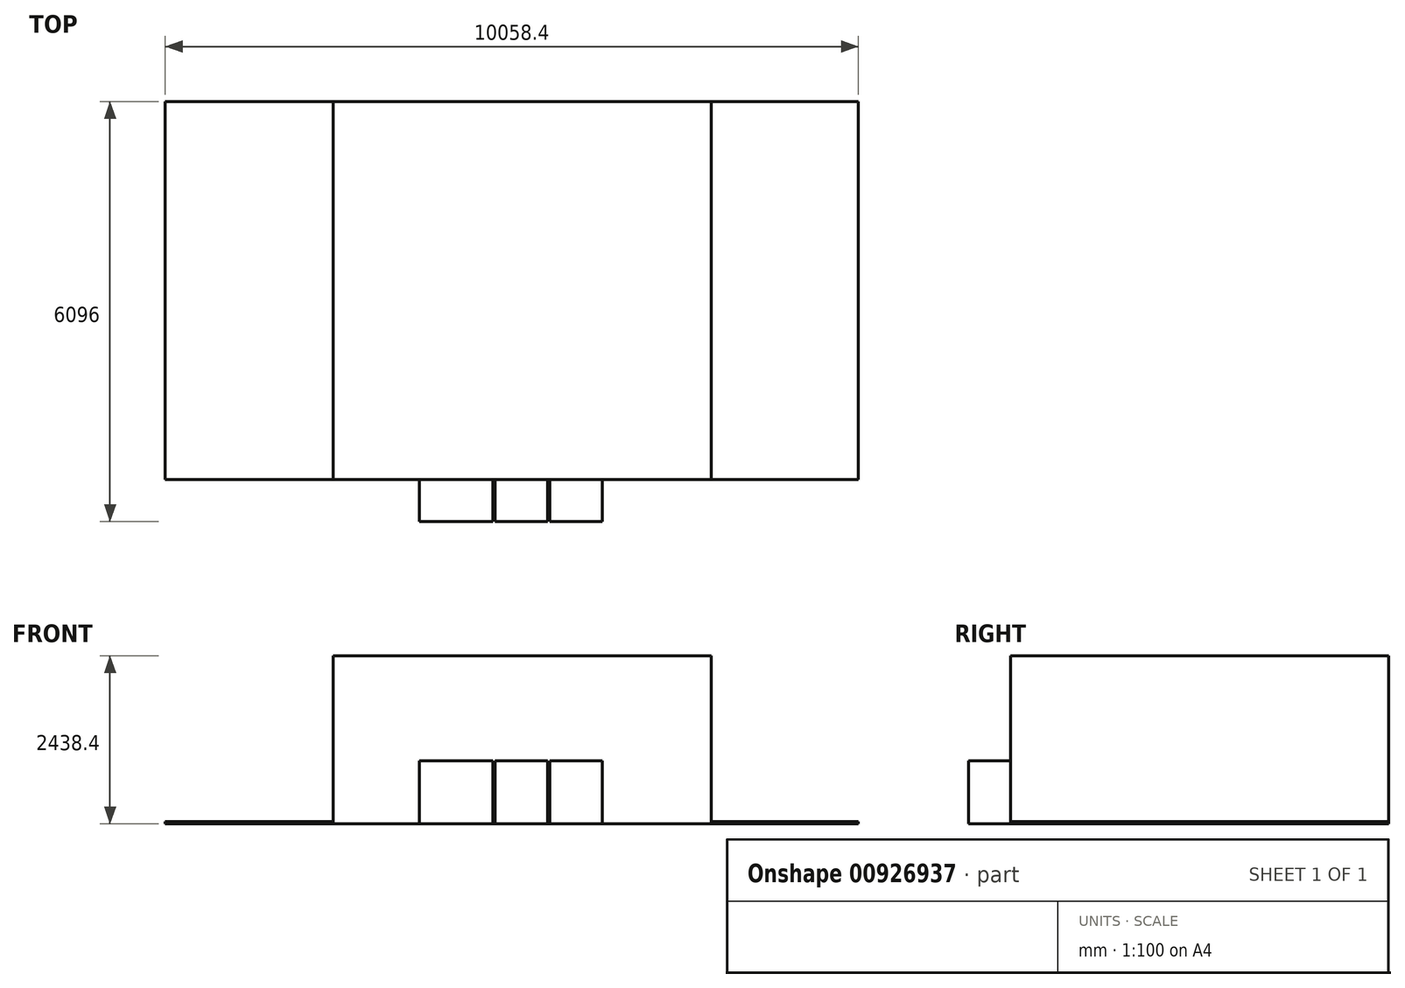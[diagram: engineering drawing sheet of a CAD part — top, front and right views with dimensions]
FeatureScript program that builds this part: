
annotation { "Feature Type Name" : "Feature", "Feature Type Description" : "" }
export const myFeature = defineFeature(function(context is Context, id is Id, definition is map)
    precondition{}
    {
        {
            var Q0;
            Q0=qCreatedBy(makeId("Top.planeOp"),FACE);
            var sketch = newSketch(context, id + "F0", { "sketchPlane" : qUnion([Q0])});
            skLineSegment(sketch, "E0.bottom", {"start": v(2743.2, 2743.2) * mm, "end": v(-2743.2, 2743.2) * mm});
            skLineSegment(sketch, "E0.top", {"start": v(2743.2, -2743.2) * mm, "end": v(-2743.2, -2743.2) * mm});
            skLineSegment(sketch, "E0.left", {"start": v(2743.2, 2743.2) * mm, "end": v(2743.2, -2743.2) * mm});
            skLineSegment(sketch, "E0.right", {"start": v(-2743.2, 2743.2) * mm, "end": v(-2743.2, -2743.2) * mm});
            skPoint(sketch, "E0.middle", {"position": v(0, 0) * mm});
            skSolve(sketch);
        }
        {
            var Q0;
            Q0 = qSketchRegion(id + "F0", true);
            extrude(context, id + "F1", {"entities" : qUnion([Q0]), "depth" : 2438.4 * mm, "offsetDistance" : 30.48 * mm});
        }
        {
            var Q0;
            Q0=makeQuery(id+"F1.opExtrude","SWEPT_FACE",FACE,{"disambiguationData":[OSD([sQuery(id+"F0.wireOp",EDGE,"E0.top")])]});
            var sketch = newSketch(context, id + "F2", { "sketchPlane" : qUnion([Q0])});
            skLineSegment(sketch, "E1", {"start": v(-2743.2, 0) * mm, "end": v(-1524, 0) * mm, "construction": true});
            skLineSegment(sketch, "E2", {"start": v(-1524, 0) * mm, "end": v(-1493.52, 0) * mm, "construction": true});
            skLineSegment(sketch, "E3", {"start": v(-1493.52, 0) * mm, "end": v(-426.72, 0) * mm});
            skLineSegment(sketch, "E4", {"start": v(-426.72, 0) * mm, "end": v(-396.24, 0) * mm, "construction": true});
            skLineSegment(sketch, "E5", {"start": v(-396.24, 0) * mm, "end": v(365.76, 0) * mm});
            skLineSegment(sketch, "E6", {"start": v(365.76, 0) * mm, "end": v(396.24, 0) * mm, "construction": true});
            skLineSegment(sketch, "E7", {"start": v(396.24, 0) * mm, "end": v(1158.24, 0) * mm});
            skLineSegment(sketch, "E8", {"start": v(-1524, 0) * mm, "end": v(1219.2, 0) * mm, "construction": true});
            skLineSegment(sketch, "E9", {"start": v(-1493.52, 0) * mm, "end": v(-1493.52, 914.4) * mm});
            skLineSegment(sketch, "E10", {"start": v(-1493.52, 914.4) * mm, "end": v(-426.72, 914.4) * mm});
            skLineSegment(sketch, "E11", {"start": v(-426.72, 914.4) * mm, "end": v(-426.72, 0) * mm});
            skLineSegment(sketch, "E12", {"start": v(-396.24, 0) * mm, "end": v(-396.24, 914.4) * mm});
            skLineSegment(sketch, "E13", {"start": v(-396.24, 914.4) * mm, "end": v(365.76, 914.4) * mm});
            skLineSegment(sketch, "E14", {"start": v(365.76, 914.4) * mm, "end": v(365.76, 0) * mm});
            skLineSegment(sketch, "E15", {"start": v(396.24, 0) * mm, "end": v(396.24, 914.4) * mm});
            skLineSegment(sketch, "E16", {"start": v(396.24, 914.4) * mm, "end": v(1158.24, 914.4) * mm});
            skLineSegment(sketch, "E17", {"start": v(1158.24, 914.4) * mm, "end": v(1158.24, 0) * mm});
            skSolve(sketch);
        }
        {
            var Q0;
            Q0 = qSketchRegion(id + "F2", true);
            extrude(context, id + "F3", {"entities" : qUnion([Q0]), "operationType" : NewBodyOperationType.ADD, "depth" : 609.6 * mm, "offsetDistance" : 30.48 * mm});
        }
        {
            var Q0;
            Q0=makeQuery(id+"F3.boolean.opBoolean","MERGE",FACE,{"derivedFrom":[makeQuery(id+"F1.opExtrude","CAP_FACE",FACE,{"disambiguationData":[OSD([sQuery(id+"F0.wireOp",EDGE,"E0.bottom"),sQuery(id+"F0.wireOp",EDGE,"E0.top"),sQuery(id+"F0.wireOp",EDGE,"E0.left"),sQuery(id+"F0.wireOp",EDGE,"E0.right")])],"isStart":true}),makeQuery(id+"F3.opExtrude","SWEPT_FACE",FACE,{"disambiguationData":[OSD([sQuery(id+"F2.wireOp",EDGE,"E3")])]}),makeQuery(id+"F3.opExtrude","SWEPT_FACE",FACE,{"disambiguationData":[OSD([sQuery(id+"F2.wireOp",EDGE,"E5")])]}),makeQuery(id+"F3.opExtrude","SWEPT_FACE",FACE,{"disambiguationData":[OSD([sQuery(id+"F2.wireOp",EDGE,"E7")])]})]});
            var sketch = newSketch(context, id + "F4", { "sketchPlane" : qUnion([Q0])});
            skLineSegment(sketch, "E18", {"start": v(2743.2, 2743.2) * mm, "end": v(4876.8, 2743.2) * mm});
            skLineSegment(sketch, "E19", {"start": v(4876.8, 2743.2) * mm, "end": v(4876.8, -2743.2) * mm});
            skLineSegment(sketch, "E20", {"start": v(4876.8, -2743.2) * mm, "end": v(2743.2, -2743.2) * mm});
            skLineSegment(sketch, "E21", {"start": v(-2743.2, -2743.2) * mm, "end": v(-5181.6, -2743.2) * mm});
            skLineSegment(sketch, "E22", {"start": v(-5181.6, -2743.2) * mm, "end": v(-5181.6, 2743.2) * mm});
            skLineSegment(sketch, "E23", {"start": v(-5181.6, 2743.2) * mm, "end": v(-2743.2, 2743.2) * mm});
            skSolve(sketch);
        }
        {
            var Q0;
            Q0 = qSketchRegion(id + "F4", true);
            var Q1;
            Q1=makeQuery(id+"F4.imprint","IMPRINT",FACE,{"disambiguationData":[TD([[makeQuery(id+"F4.imprint","IMPRINT",EDGE,{"derivedFrom":sQuery(id+"F4.wireOp",EDGE,"E21")}),-1.0]])]});
            var Q2;
            Q2=makeQuery(id+"F4.imprint","IMPRINT",FACE,{"disambiguationData":[TD([[makeQuery(id+"F4.imprint","IMPRINT",EDGE,{"derivedFrom":sQuery(id+"F4.wireOp",EDGE,"E18")}),-1.0]])]});
            extrude(context, id + "F5", {"entities" : qUnion([Q0, Q1, Q2]), "oppositeDirection" : true, "depth" : 30.48 * mm, "offsetDistance" : 30.48 * mm});
        }
    });
